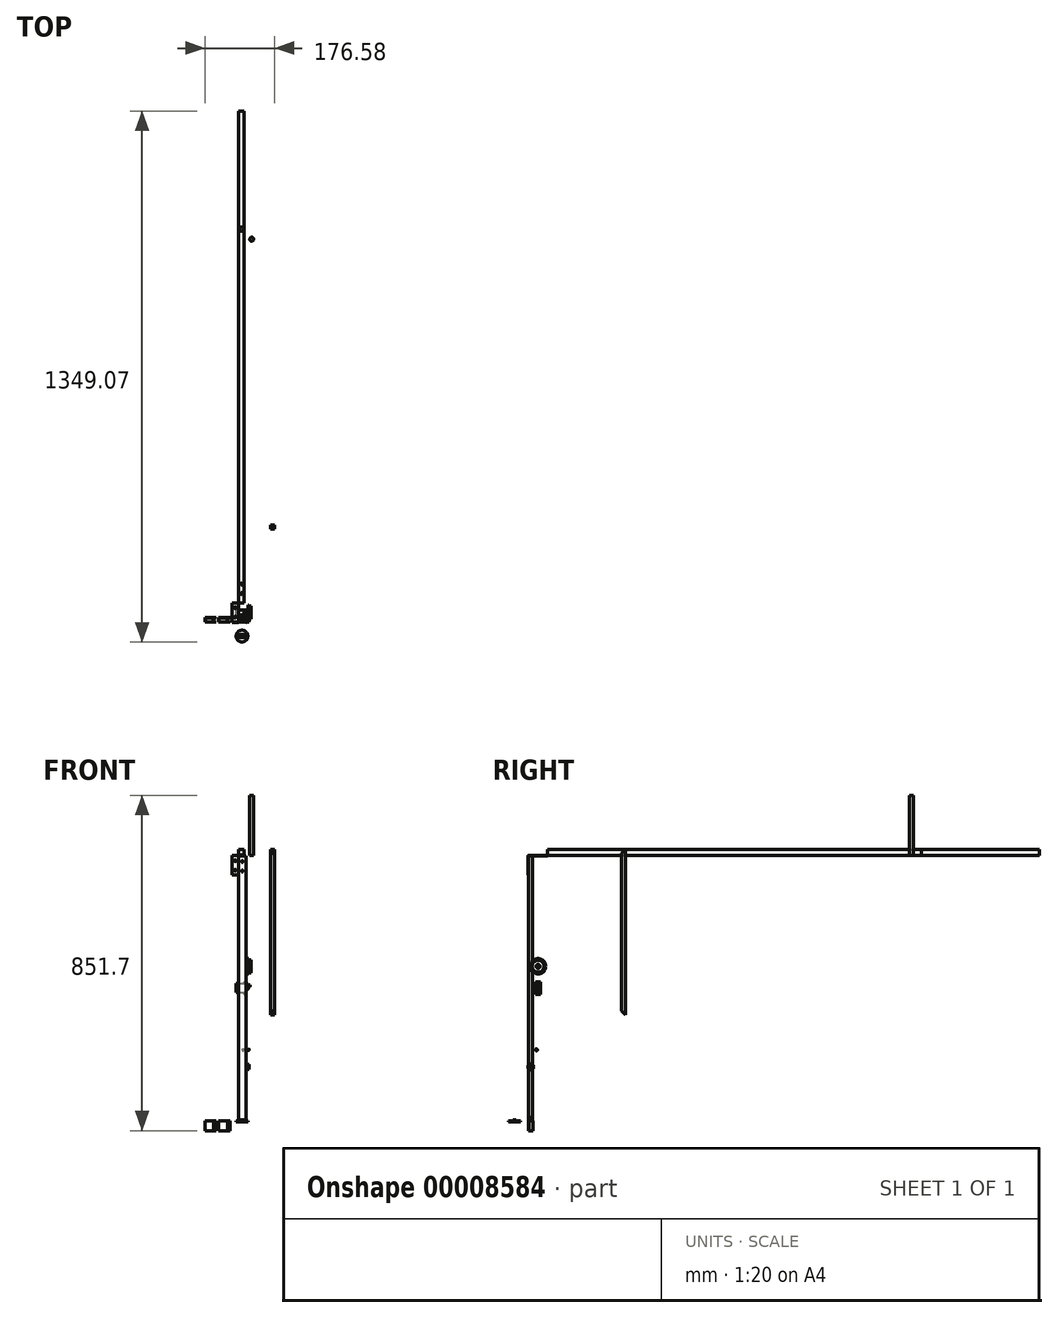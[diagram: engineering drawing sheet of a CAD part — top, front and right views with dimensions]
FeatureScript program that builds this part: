
annotation { "Feature Type Name" : "Feature", "Feature Type Description" : "" }
export const myFeature = defineFeature(function(context is Context, id is Id, definition is map)
    precondition{}
    {
        {
            var Q0;
            Q0=qCreatedBy(makeId("Front.planeOp"),FACE);
            var sketch = newSketch(context, id + "F0", { "sketchPlane" : qUnion([Q0])});
            skLineSegment(sketch, "E0.rect.bottom", {"start": v(-7.5, 7.5) * mm, "end": v(7.5, 7.5) * mm});
            skLineSegment(sketch, "E0.rect.top", {"start": v(-7.5, -7.5) * mm, "end": v(7.5, -7.5) * mm});
            skLineSegment(sketch, "E0.rect.left", {"start": v(-7.5, 7.5) * mm, "end": v(-7.5, -7.5) * mm});
            skLineSegment(sketch, "E0.rect.right", {"start": v(7.5, 7.5) * mm, "end": v(7.5, -7.5) * mm});
            skPoint(sketch, "E0.rect.middle", {"position": v(0, 0) * mm});
            skLineSegment(sketch, "E1.rect.bottom", {"start": v(-7, 7) * mm, "end": v(7, 7) * mm});
            skLineSegment(sketch, "E1.rect.top", {"start": v(-7, -7) * mm, "end": v(7, -7) * mm});
            skLineSegment(sketch, "E1.rect.left", {"start": v(-7, 7) * mm, "end": v(-7, -7) * mm});
            skLineSegment(sketch, "E1.rect.right", {"start": v(7, 7) * mm, "end": v(7, -7) * mm});
            skSolve(sketch);
        }
        {
            var Q0;
            Q0 = qSketchRegion(id + "F0", true);
            extrude(context, id + "F1", {"entities" : qUnion([Q0]), "depth" : 950 * mm});
        }
        {
            var Q0;
            Q0=makeQuery(id+"F1.opExtrude","SWEPT_FACE",FACE,{"disambiguationData":[OSD([sQuery(id+"F0.wireOp",EDGE,"E0.rect.left")])]});
            var sketch = newSketch(context, id + "F2", { "sketchPlane" : qUnion([Q0])});
            skLineSegment(sketch, "E2.bottom", {"start": v(998.04, -7.5) * mm, "end": v(950, -7.5) * mm});
            skLineSegment(sketch, "E2.top", {"start": v(998, -9.5) * mm, "end": v(950, -9.5) * mm});
            skLineSegment(sketch, "E2.right", {"start": v(950, -7.5) * mm, "end": v(950, -9.5) * mm});
            skLineSegment(sketch, "E3.top", {"start": v(1000, -57.5) * mm, "end": v(998, -57.5) * mm});
            skLineSegment(sketch, "E3.left", {"start": v(1000, -9.5) * mm, "end": v(1000, -57.5) * mm});
            skLineSegment(sketch, "E3.right", {"start": v(998, -9.5) * mm, "end": v(998, -57.5) * mm});
            skArc(sketch, "E4", {"start": v(1000, -9.5) * mm, "mid": v(999.4, -8.07) * mm, "end": v(997.96, -7.5) * mm});
            skSolve(sketch);
        }
        {
            var Q0;
            Q0 = qSketchRegion(id + "F2", true);
            extrude(context, id + "F3", {"entities" : qUnion([Q0]), "depth" : 16.4 * mm});
        }
        {
            var Q0;
            Q0=makeQuery(id+"F3.opExtrude","SWEPT_FACE",FACE,{"disambiguationData":[OSD([sQuery(id+"F2.wireOp",EDGE,"E3.left")])]});
            var sketch = newSketch(context, id + "F4", { "sketchPlane" : qUnion([Q0])});
            skCircle(sketch, "E5", {"center": v(-15.7, -21.5) * mm, "radius": 2.3 * mm});
            skCircle(sketch, "E6", {"center": v(-15.7, -45.5) * mm, "radius": 2.3 * mm});
            skSolve(sketch);
        }
        {
            var Q0;
            Q0 = qSketchRegion(id + "F4", true);
            extrude(context, id + "F5", {"entities" : qUnion([Q0]), "operationType" : NewBodyOperationType.REMOVE, "oppositeDirection" : true, "depth" : 25 * mm});
        }
        {
            var Q0;
            Q0=makeQuery(id+"F3.opExtrude","SWEPT_FACE",FACE,{"disambiguationData":[OSD([sQuery(id+"F2.wireOp",EDGE,"E2.bottom")])]});
            var sketch = newSketch(context, id + "F6", { "sketchPlane" : qUnion([Q0])});
            skCircle(sketch, "E7", {"center": v(0, 12) * mm, "radius": 2.3 * mm});
            skCircle(sketch, "E8", {"center": v(0, -12) * mm, "radius": 2.3 * mm});
            skCircle(sketch, "E9", {"center": v(-15.7, -985.97) * mm, "radius": 2.3 * mm});
            skCircle(sketch, "E10", {"center": v(-15.7, -961.99) * mm, "radius": 2.3 * mm});
            skSolve(sketch);
        }
        {
            var Q0;
            Q0=makeQuery(id+"F6.imprint","IMPRINT",FACE,{"disambiguationData":[TD([[makeQuery(id+"F6.imprint","IMPRINT",EDGE,{"derivedFrom":sQuery(id+"F6.wireOp",EDGE,"E9")}),1.0]])]});
            var Q1;
            Q1=makeQuery(id+"F6.imprint","IMPRINT",FACE,{"disambiguationData":[TD([[makeQuery(id+"F6.imprint","IMPRINT",EDGE,{"derivedFrom":sQuery(id+"F6.wireOp",EDGE,"E10")}),1.0]])]});
            extrude(context, id + "F7", {"entities" : qUnion([Q0, Q1]), "operationType" : NewBodyOperationType.REMOVE, "oppositeDirection" : true, "depth" : 3 * mm});
        }
        {
            var Q0;
            Q0=makeQuery(id+"F3.opExtrude","SWEPT_FACE",FACE,{"disambiguationData":[OSD([sQuery(id+"F2.wireOp",EDGE,"E2.top")])]});
            var sketch = newSketch(context, id + "F8", { "sketchPlane" : qUnion([Q0])});
            skLineSegment(sketch, "E11.bottom", {"start": v(-7.5, 998) * mm, "end": v(12.5, 998) * mm});
            skLineSegment(sketch, "E11.top", {"start": v(-7.5, 988) * mm, "end": v(12.5, 988) * mm});
            skLineSegment(sketch, "E11.left", {"start": v(-7.5, 998) * mm, "end": v(-7.5, 988) * mm});
            skLineSegment(sketch, "E11.right", {"start": v(12.5, 998) * mm, "end": v(12.5, 988) * mm});
            skLineSegment(sketch, "E12.rect.bottom", {"start": v(-6.75, 988.75) * mm, "end": v(11.75, 988.75) * mm});
            skLineSegment(sketch, "E12.rect.top", {"start": v(-6.75, 997.25) * mm, "end": v(11.75, 997.25) * mm});
            skLineSegment(sketch, "E12.rect.left", {"start": v(-6.75, 988.75) * mm, "end": v(-6.75, 997.25) * mm});
            skLineSegment(sketch, "E12.rect.right", {"start": v(11.75, 988.75) * mm, "end": v(11.75, 997.25) * mm});
            skPoint(sketch, "E12.rect.middle", {"position": v(2.5, 993) * mm});
            skSolve(sketch);
        }
        {
            var Q0;
            Q0=makeQuery(id+"F8.imprint","IMPRINT",FACE,{"disambiguationData":[TD([[makeQuery(id+"F8.imprint","IMPRINT",EDGE,{"derivedFrom":sQuery(id+"F8.wireOp",EDGE,"E11.bottom")}),-1.0]])]});
            extrude(context, id + "F9", {"entities" : qUnion([Q0]), "depth" : 673 * mm});
        }
        {
            var Q0;
            Q0=makeQuery(id+"F9.opExtrude","SWEPT_FACE",FACE,{"disambiguationData":[OSD([sQuery(id+"F8.wireOp",EDGE,"E11.bottom")])]});
            var sketch = newSketch(context, id + "F10", { "sketchPlane" : qUnion([Q0])});
            skCircle(sketch, "E13", {"center": v(2.5, -23.5) * mm, "radius": 2.3 * mm});
            skCircle(sketch, "E14", {"center": v(2.5, -47.5) * mm, "radius": 2.3 * mm});
            skSolve(sketch);
        }
        {
            var Q0;
            Q0 = qSketchRegion(id + "F10", true);
            extrude(context, id + "F11", {"entities" : qUnion([Q0]), "operationType" : NewBodyOperationType.REMOVE, "oppositeDirection" : true, "depth" : 11 * mm});
        }
        {
            var Q0;
            Q0=makeQuery(id+"F1.opExtrude","SWEPT_FACE",FACE,{"disambiguationData":[OSD([sQuery(id+"F0.wireOp",EDGE,"E0.rect.top")])]});
            var sketch = newSketch(context, id + "F12", { "sketchPlane" : qUnion([Q0])});
            skCircle(sketch, "E15", {"center": v(0, 901.99) * mm, "radius": 2.3 * mm});
            skCircle(sketch, "E16", {"center": v(0, 925.97) * mm, "radius": 2.3 * mm});
            skLineSegment(sketch, "E17", {"start": v(0, 950) * mm, "end": v(0, 925.97) * mm});
            skLineSegment(sketch, "E18", {"start": v(0, 925.97) * mm, "end": v(0, 901.99) * mm});
            skSolve(sketch);
        }
        {
            var Q0;
            Q0=makeQuery(id+"F12.imprint","IMPRINT",FACE,{"disambiguationData":[TD([[makeQuery(id+"F12.imprint","IMPRINT",EDGE,{"derivedFrom":sQuery(id+"F12.wireOp",EDGE,"E15")}),1.0]])]});
            var Q1;
            Q1=makeQuery(id+"F12.imprint","IMPRINT",FACE,{"disambiguationData":[TD([[makeQuery(id+"F12.imprint","IMPRINT",EDGE,{"derivedFrom":sQuery(id+"F12.wireOp",EDGE,"E16")}),1.0]])]});
            extrude(context, id + "F13", {"entities" : qUnion([Q0, Q1]), "operationType" : NewBodyOperationType.REMOVE, "oppositeDirection" : true, "depth" : 25 * mm});
        }
        {
            var Q0;
            Q0=makeQuery(id+"F9.opExtrude","CAP_FACE",FACE,{"disambiguationData":[OSD([sQuery(id+"F8.wireOp",EDGE,"E11.bottom"),sQuery(id+"F8.wireOp",EDGE,"E11.top"),sQuery(id+"F8.wireOp",EDGE,"E11.left"),sQuery(id+"F8.wireOp",EDGE,"E11.right"),sQuery(id+"F8.wireOp",EDGE,"E12.rect.bottom"),sQuery(id+"F8.wireOp",EDGE,"E12.rect.top"),sQuery(id+"F8.wireOp",EDGE,"E12.rect.left"),sQuery(id+"F8.wireOp",EDGE,"E12.rect.right")])],"isStart":false});
            var sketch = newSketch(context, id + "F14", { "sketchPlane" : qUnion([Q0])});
            skCircle(sketch, "E19", {"center": v(1.66, 1034.07) * mm, "radius": 15 * mm});
            skSolve(sketch);
        }
        {
            var Q0;
            Q0 = qSketchRegion(id + "F14", true);
            extrude(context, id + "F15", {"entities" : qUnion([Q0]), "depth" : 2 * mm});
        }
        {
            var Q0;
            Q0=makeQuery(id+"F15.opExtrude","CAP_FACE",FACE,{"disambiguationData":[OSD([sQuery(id+"F14.wireOp",EDGE,"E19")])],"isStart":true});
            var sketch = newSketch(context, id + "F16", { "sketchPlane" : qUnion([Q0])});
            skLineSegment(sketch, "E20.rect.bottom", {"start": v(-7.59, -1038.32) * mm, "end": v(10.91, -1038.32) * mm});
            skLineSegment(sketch, "E20.rect.top", {"start": v(-7.59, -1029.82) * mm, "end": v(10.91, -1029.82) * mm});
            skLineSegment(sketch, "E20.rect.left", {"start": v(-7.59, -1038.32) * mm, "end": v(-7.59, -1029.82) * mm});
            skLineSegment(sketch, "E20.rect.right", {"start": v(10.91, -1038.32) * mm, "end": v(10.91, -1029.82) * mm});
            skPoint(sketch, "E20.rect.middle", {"position": v(1.66, -1034.07) * mm});
            skSolve(sketch);
        }
        {
            var Q0;
            Q0 = qSketchRegion(id + "F16", true);
            extrude(context, id + "F17", {"entities" : qUnion([Q0]), "operationType" : NewBodyOperationType.ADD, "depth" : 3 * mm});
        }
        {
            var Q0;
            Q0=makeQuery(id+"F9.opExtrude","CAP_FACE",FACE,{"disambiguationData":[OSD([sQuery(id+"F8.wireOp",EDGE,"E11.bottom"),sQuery(id+"F8.wireOp",EDGE,"E11.top"),sQuery(id+"F8.wireOp",EDGE,"E11.left"),sQuery(id+"F8.wireOp",EDGE,"E11.right"),sQuery(id+"F8.wireOp",EDGE,"E12.rect.bottom"),sQuery(id+"F8.wireOp",EDGE,"E12.rect.top"),sQuery(id+"F8.wireOp",EDGE,"E12.rect.left"),sQuery(id+"F8.wireOp",EDGE,"E12.rect.right")])],"isStart":false});
            var sketch = newSketch(context, id + "F18", { "sketchPlane" : qUnion([Q0])});
            skLineSegment(sketch, "E21.rect.bottom", {"start": v(-56.56, 987.8) * mm, "end": v(-36.56, 987.8) * mm});
            skLineSegment(sketch, "E21.rect.top", {"start": v(-56.56, 997.8) * mm, "end": v(-36.56, 997.8) * mm});
            skLineSegment(sketch, "E21.rect.left", {"start": v(-56.56, 987.8) * mm, "end": v(-56.56, 997.8) * mm});
            skLineSegment(sketch, "E21.rect.right", {"start": v(-36.56, 987.8) * mm, "end": v(-36.56, 997.8) * mm});
            skPoint(sketch, "E21.rect.middle", {"position": v(-46.56, 992.8) * mm});
            skLineSegment(sketch, "E22.rect.bottom", {"start": v(-91.4, 987.8) * mm, "end": v(-71.4, 987.8) * mm});
            skLineSegment(sketch, "E22.rect.top", {"start": v(-91.4, 997.8) * mm, "end": v(-71.4, 997.8) * mm});
            skLineSegment(sketch, "E22.rect.left", {"start": v(-91.4, 987.8) * mm, "end": v(-91.4, 997.8) * mm});
            skLineSegment(sketch, "E22.rect.right", {"start": v(-71.4, 987.8) * mm, "end": v(-71.4, 997.8) * mm});
            skPoint(sketch, "E22.rect.middle", {"position": v(-81.4, 992.8) * mm});
            skLineSegment(sketch, "E23.rect.bottom", {"start": v(-92.4, 986.8) * mm, "end": v(-70.4, 986.8) * mm});
            skLineSegment(sketch, "E23.rect.top", {"start": v(-92.4, 998.8) * mm, "end": v(-70.4, 998.8) * mm});
            skLineSegment(sketch, "E23.rect.left", {"start": v(-92.4, 986.8) * mm, "end": v(-92.4, 998.8) * mm});
            skLineSegment(sketch, "E23.rect.right", {"start": v(-70.4, 986.8) * mm, "end": v(-70.4, 998.8) * mm});
            skLineSegment(sketch, "E24.rect.bottom", {"start": v(-57.56, 986.8) * mm, "end": v(-35.56, 986.8) * mm});
            skLineSegment(sketch, "E24.rect.top", {"start": v(-57.56, 998.8) * mm, "end": v(-35.56, 998.8) * mm});
            skLineSegment(sketch, "E24.rect.left", {"start": v(-57.56, 986.8) * mm, "end": v(-57.56, 998.8) * mm});
            skLineSegment(sketch, "E24.rect.right", {"start": v(-35.56, 986.8) * mm, "end": v(-35.56, 998.8) * mm});
            skSolve(sketch);
        }
        {
            var Q0;
            Q0 = qSketchRegion(id + "F18", true);
            extrude(context, id + "F19", {"entities" : qUnion([Q0]), "depth" : 24.7 * mm});
        }
        {
            var Q0;
            Q0=makeQuery(id+"F19.opExtrude","SWEPT_FACE",FACE,{"disambiguationData":[OSD([sQuery(id+"F18.wireOp",EDGE,"E23.rect.bottom")])]});
            var sketch = newSketch(context, id + "F20", { "sketchPlane" : qUnion([Q0])});
            skLineSegment(sketch, "E25", {"start": v(81.4, -528.03) * mm, "end": v(87.58, -521.85) * mm});
            skLineSegment(sketch, "E26", {"start": v(87.58, -521.85) * mm, "end": v(81.4, -515.68) * mm});
            skLineSegment(sketch, "E27", {"start": v(81.4, -515.68) * mm, "end": v(75.23, -521.85) * mm});
            skLineSegment(sketch, "E28", {"start": v(75.23, -521.85) * mm, "end": v(81.4, -528.03) * mm});
            skSolve(sketch);
        }
        {
            var Q0;
            Q0 = qSketchRegion(id + "F20", true);
            extrude(context, id + "F21", {"entities" : qUnion([Q0]), "operationType" : NewBodyOperationType.REMOVE, "oppositeDirection" : true, "depth" : 25 * mm});
        }
        {
            var Q0;
            Q0=makeQuery(id+"F19.opExtrude","CAP_FACE",FACE,{"disambiguationData":[OSD([sQuery(id+"F18.wireOp",EDGE,"E22.rect.bottom"),sQuery(id+"F18.wireOp",EDGE,"E22.rect.top"),sQuery(id+"F18.wireOp",EDGE,"E22.rect.left"),sQuery(id+"F18.wireOp",EDGE,"E22.rect.right"),sQuery(id+"F18.wireOp",EDGE,"E23.rect.bottom"),sQuery(id+"F18.wireOp",EDGE,"E23.rect.top"),sQuery(id+"F18.wireOp",EDGE,"E23.rect.left"),sQuery(id+"F18.wireOp",EDGE,"E23.rect.right")])],"isStart":false});
            var sketch = newSketch(context, id + "F22", { "sketchPlane" : qUnion([Q0])});
            skLineSegment(sketch, "E29", {"start": v(-70.4, 998.8) * mm, "end": v(-63.9, 998.8) * mm});
            skLineSegment(sketch, "E30", {"start": v(-63.9, 998.8) * mm, "end": v(-63.9, 997.8) * mm});
            skLineSegment(sketch, "E31", {"start": v(-63.9, 997.8) * mm, "end": v(-70.4, 997.8) * mm});
            skLineSegment(sketch, "E32", {"start": v(-70.4, 986.8) * mm, "end": v(-63.9, 986.8) * mm});
            skLineSegment(sketch, "E33", {"start": v(-63.9, 986.8) * mm, "end": v(-63.9, 987.8) * mm});
            skLineSegment(sketch, "E34", {"start": v(-63.9, 987.8) * mm, "end": v(-70.4, 987.8) * mm});
            skLineSegment(sketch, "E35", {"start": v(-35.56, 998.8) * mm, "end": v(-29.06, 998.8) * mm});
            skLineSegment(sketch, "E36", {"start": v(-29.06, 998.8) * mm, "end": v(-29.06, 997.8) * mm});
            skLineSegment(sketch, "E37", {"start": v(-29.06, 997.8) * mm, "end": v(-35.56, 997.8) * mm});
            skLineSegment(sketch, "E38", {"start": v(-35.56, 986.8) * mm, "end": v(-29.06, 986.8) * mm});
            skLineSegment(sketch, "E39", {"start": v(-29.06, 986.8) * mm, "end": v(-29.06, 987.8) * mm});
            skLineSegment(sketch, "E40", {"start": v(-29.06, 987.8) * mm, "end": v(-35.56, 987.8) * mm});
            skLineSegment(sketch, "E41", {"start": v(-70.4, 998.8) * mm, "end": v(-70.4, 997.8) * mm});
            skLineSegment(sketch, "E42", {"start": v(-70.4, 987.8) * mm, "end": v(-70.4, 986.8) * mm});
            skLineSegment(sketch, "E43", {"start": v(-35.56, 987.8) * mm, "end": v(-35.56, 986.8) * mm});
            skLineSegment(sketch, "E44", {"start": v(-35.56, 998.8) * mm, "end": v(-35.56, 997.8) * mm});
            skSolve(sketch);
        }
        {
            var Q0;
            Q0 = qSketchRegion(id + "F22", true);
            extrude(context, id + "F23", {"entities" : qUnion([Q0]), "oppositeDirection" : true, "depth" : 24.7 * mm});
        }
        {
            var Q0;
            Q0=makeQuery(id+"F9.opExtrude","SWEPT_FACE",FACE,{"disambiguationData":[OSD([sQuery(id+"F8.wireOp",EDGE,"E11.right")])]});
            var sketch = newSketch(context, id + "F24", { "sketchPlane" : qUnion([Q0])});
            skCircle(sketch, "E45", {"center": v(-992.74, -545.12) * mm, "radius": 7.5 * mm});
            skSolve(sketch);
        }
        {
            var Q0;
            Q0 = qSketchRegion(id + "F24", true);
            extrude(context, id + "F25", {"entities" : qUnion([Q0]), "depth" : 1.1 * mm});
        }
        {
            var Q0;
            Q0=makeQuery(id+"F25.opExtrude","CAP_FACE",FACE,{"disambiguationData":[OSD([sQuery(id+"F24.wireOp",EDGE,"E45")])],"isStart":false});
            var sketch = newSketch(context, id + "F26", { "sketchPlane" : qUnion([Q0])});
            skCircle(sketch, "E46", {"center": v(-992.74, -545.12) * mm, "radius": 5.25 * mm});
            skSolve(sketch);
        }
        {
            var Q0;
            Q0 = qSketchRegion(id + "F26", true);
            extrude(context, id + "F27", {"entities" : qUnion([Q0]), "operationType" : NewBodyOperationType.ADD, "depth" : 5.5 * mm});
        }
        {
            var Q0;
            Q0=makeQuery(id+"F27.opExtrude","CAP_FACE",FACE,{"disambiguationData":[OSD([sQuery(id+"F26.wireOp",EDGE,"E46")])],"isStart":false});
            var sketch = newSketch(context, id + "F28", { "sketchPlane" : qUnion([Q0])});
            skSolve(sketch);
        }
        {
            var Q0;
            Q0=makeQuery(id+"F28.imprint","IMPRINT",FACE,{"disambiguationData":[TD([[makeQuery(id+"F28.imprint","IMPRINT",EDGE,{"derivedFrom":makeQuery(id+"F27.opExtrude","CAP_EDGE",EDGE,{"disambiguationData":[OSD([sQuery(id+"F26.wireOp",EDGE,"E46")])],"isStart":false})}),1.0]])]});
            var sketch = newSketch(context, id + "F29", { "sketchPlane" : qUnion([Q0])});
            skCircle(sketch, "E47.0", {"center": v(-992.74, -545.12) * mm, "radius": 5.25 * mm});
            skLineSegment(sketch, "E48", {"start": v(-993.24, -539.89) * mm, "end": v(-992.32, -539.88) * mm});
            skLineSegment(sketch, "E49", {"start": v(-992.32, -539.88) * mm, "end": v(-992.53, -539.3) * mm});
            skLineSegment(sketch, "E50", {"start": v(-992.53, -539.3) * mm, "end": v(-993.01, -539.3) * mm});
            skLineSegment(sketch, "E51", {"start": v(-993.01, -539.3) * mm, "end": v(-993.24, -539.89) * mm});
            skSolve(sketch);
        }
        {
            var Q0;
            {var subQ1=sQuery(id+"F29.wireOp",EDGE,"E49");Q0=makeQuery(id+"F29.imprint","IMPRINT",FACE,{"disambiguationData":[TD([[makeQuery(id+"F29.imprint","IMPRINT",EDGE,{"derivedFrom":subQ1}),1.0]])]});}
            extrude(context, id + "F30", {"entities" : qUnion([Q0]), "oppositeDirection" : true, "depth" : 5.5 * mm});
        }
        {
            var Q0;
            Q0=makeQuery(id+"F30.opExtrude","SWEPT_BODY",BODY,{"disambiguationData":[OSD([sQuery(id+"F29.wireOp",EDGE,"E47.0"),sQuery(id+"F29.wireOp",EDGE,"E49"),sQuery(id+"F29.wireOp",EDGE,"E50"),sQuery(id+"F29.wireOp",EDGE,"E51")])]});
            var Q1;
            Q1=makeQuery(id+"F27.opExtrude","CAP_EDGE",EDGE,{"disambiguationData":[OSD([sQuery(id+"F26.wireOp",EDGE,"E46")])],"isStart":false});
            circularPattern(context, id + "F31", {"entities" : qUnion([Q0]), "axis" : qUnion([Q1]), "angle" : 10 * degree, "instanceCount" : 40, "computeTransformsWithoutBuiltin" : true});
        }
        {
            var Q0;
            Q0=makeQuery(id+"F25.opExtrude","CAP_FACE",FACE,{"disambiguationData":[OSD([sQuery(id+"F24.wireOp",EDGE,"E45")])],"isStart":true});
            var sketch = newSketch(context, id + "F32", { "sketchPlane" : qUnion([Q0])});
            skCircle(sketch, "E52", {"center": v(992.74, -545.12) * mm, "radius": 1.5 * mm});
            skSolve(sketch);
        }
        {
            var Q0;
            Q0 = qSketchRegion(id + "F32", true);
            extrude(context, id + "F33", {"entities" : qUnion([Q0]), "operationType" : NewBodyOperationType.REMOVE, "oppositeDirection" : true, "depth" : 25 * mm});
        }
        {
            var Q0;
            Q0=makeQuery(id+"F9.opExtrude","SWEPT_FACE",FACE,{"disambiguationData":[OSD([sQuery(id+"F8.wireOp",EDGE,"E11.right")])]});
            var sketch = newSketch(context, id + "F34", { "sketchPlane" : qUnion([Q0])});
            skLineSegment(sketch, "E53.bottom", {"start": v(-980.2, -333.62) * mm, "end": v(-968.2, -333.62) * mm});
            skLineSegment(sketch, "E53.top", {"start": v(-980.2, -356.12) * mm, "end": v(-968.2, -356.12) * mm});
            skLineSegment(sketch, "E53.left", {"start": v(-980.2, -333.62) * mm, "end": v(-980.2, -356.12) * mm});
            skLineSegment(sketch, "E53.right", {"start": v(-968.2, -333.62) * mm, "end": v(-968.2, -356.12) * mm});
            skSolve(sketch);
        }
        {
            var Q0;
            Q0 = qSketchRegion(id + "F34", true);
            extrude(context, id + "F35", {"entities" : qUnion([Q0]), "oppositeDirection" : true, "depth" : 26.5 * mm});
        }
        {
            var Q0;
            Q0=makeQuery(id+"F35.opExtrude","SWEPT_FACE",FACE,{"disambiguationData":[OSD([sQuery(id+"F34.wireOp",EDGE,"E53.right")])]});
            var sketch = newSketch(context, id + "F36", { "sketchPlane" : qUnion([Q0])});
            skLineSegment(sketch, "E54.bottom", {"start": v(-7, -356.12) * mm, "end": v(-8.5, -356.12) * mm});
            skLineSegment(sketch, "E54.top", {"start": v(-7, -361.12) * mm, "end": v(-8.5, -361.12) * mm});
            skLineSegment(sketch, "E54.left", {"start": v(-7, -356.12) * mm, "end": v(-7, -361.12) * mm});
            skLineSegment(sketch, "E54.right", {"start": v(-8.5, -356.12) * mm, "end": v(-8.5, -361.12) * mm});
            skLineSegment(sketch, "E55.bottom", {"start": v(-7, -333.62) * mm, "end": v(-8.5, -333.62) * mm});
            skLineSegment(sketch, "E55.top", {"start": v(-7, -328.62) * mm, "end": v(-8.5, -328.62) * mm});
            skLineSegment(sketch, "E55.left", {"start": v(-7, -333.62) * mm, "end": v(-7, -328.62) * mm});
            skLineSegment(sketch, "E55.right", {"start": v(-8.5, -333.62) * mm, "end": v(-8.5, -328.62) * mm});
            skSolve(sketch);
        }
        {
            var Q0;
            Q0 = qSketchRegion(id + "F36", true);
            extrude(context, id + "F37", {"entities" : qUnion([Q0]), "oppositeDirection" : true, "depth" : 12 * mm});
        }
        {
            var Q0;
            Q0=makeQuery(id+"F35.opExtrude","CAP_FACE",FACE,{"disambiguationData":[OSD([sQuery(id+"F34.wireOp",EDGE,"E53.bottom"),sQuery(id+"F34.wireOp",EDGE,"E53.top"),sQuery(id+"F34.wireOp",EDGE,"E53.left"),sQuery(id+"F34.wireOp",EDGE,"E53.right")])],"isStart":true});
            var sketch = newSketch(context, id + "F38", { "sketchPlane" : qUnion([Q0])});
            skLineSegment(sketch, "E56", {"start": v(-974.2, -333.62) * mm, "end": v(-974.2, -356.12) * mm});
            skCircle(sketch, "E57", {"center": v(-974.2, -339.6) * mm, "radius": 5.72 * mm});
            skSolve(sketch);
        }
        {
            var Q0;
            Q0 = qSketchRegion(id + "F38", true);
            extrude(context, id + "F39", {"entities" : qUnion([Q0]), "operationType" : NewBodyOperationType.ADD, "depth" : 4.5 * mm});
        }
        {
            var Q0;
            Q0=makeQuery(id+"F39.opExtrude","CAP_FACE",FACE,{"disambiguationData":[OSD([sQuery(id+"F38.wireOp",EDGE,"E57")])],"isStart":false});
            var sketch = newSketch(context, id + "F40", { "sketchPlane" : qUnion([Q0])});
            skCircle(sketch, "E58", {"center": v(-974.2, -339.6) * mm, "radius": 2 * mm});
            skSolve(sketch);
        }
        {
            var Q0;
            Q0 = qSketchRegion(id + "F40", true);
            extrude(context, id + "F41", {"entities" : qUnion([Q0]), "operationType" : NewBodyOperationType.ADD, "depth" : 4.5 * mm});
        }
        {
            var Q0;
            Q0=makeQuery(id+"F41.opExtrude","CAP_FACE",FACE,{"disambiguationData":[OSD([sQuery(id+"F40.wireOp",EDGE,"E58")])],"isStart":false});
            var sketch = newSketch(context, id + "F42", { "sketchPlane" : qUnion([Q0])});
            skLineSegment(sketch, "E59", {"start": v(-973.99, -341.58) * mm, "end": v(-974.14, -341.98) * mm});
            skLineSegment(sketch, "E60", {"start": v(-974.14, -341.98) * mm, "end": v(-974.35, -341.98) * mm});
            skLineSegment(sketch, "E61", {"start": v(-974.35, -341.98) * mm, "end": v(-974.5, -341.57) * mm});
            skLineSegment(sketch, "E62", {"start": v(-974.5, -341.57) * mm, "end": v(-973.99, -341.58) * mm});
            skSolve(sketch);
        }
        {
            var Q0;
            Q0 = qSketchRegion(id + "F42", true);
            extrude(context, id + "F43", {"entities" : qUnion([Q0]), "oppositeDirection" : true, "depth" : 4.5 * mm});
        }
        {
            var Q0;
            Q0=makeQuery(id+"F43.opExtrude","SWEPT_BODY",BODY,{"disambiguationData":[OSD([sQuery(id+"F42.wireOp",EDGE,"E59"),sQuery(id+"F42.wireOp",EDGE,"E60"),sQuery(id+"F42.wireOp",EDGE,"E61"),sQuery(id+"F42.wireOp",EDGE,"E62")])]});
            var Q1;
            Q1=makeQuery(id+"F41.opExtrude","CAP_EDGE",EDGE,{"disambiguationData":[OSD([sQuery(id+"F40.wireOp",EDGE,"E58")])],"isStart":false});
            circularPattern(context, id + "F44", {"entities" : qUnion([Q0]), "axis" : qUnion([Q1]), "angle" : 20 * degree, "instanceCount" : 30, "computeTransformsWithoutBuiltin" : true});
        }
        {
            var Q0;
            Q0=makeQuery(id+"F35.opExtrude","SWEPT_BODY",BODY,{"disambiguationData":[OSD([sQuery(id+"F34.wireOp",EDGE,"E53.bottom"),sQuery(id+"F34.wireOp",EDGE,"E53.top"),sQuery(id+"F34.wireOp",EDGE,"E53.left"),sQuery(id+"F34.wireOp",EDGE,"E53.right")])]});
            var Q1;
            Q1=makeQuery(id+"F37.opExtrude","SWEPT_BODY",BODY,{"disambiguationData":[OSD([sQuery(id+"F36.wireOp",EDGE,"E54.bottom"),sQuery(id+"F36.wireOp",EDGE,"E54.top"),sQuery(id+"F36.wireOp",EDGE,"E54.left"),sQuery(id+"F36.wireOp",EDGE,"E54.right")])]});
            var Q2;
            Q2=makeQuery(id+"F37.opExtrude","SWEPT_BODY",BODY,{"disambiguationData":[OSD([sQuery(id+"F36.wireOp",EDGE,"E55.bottom"),sQuery(id+"F36.wireOp",EDGE,"E55.top"),sQuery(id+"F36.wireOp",EDGE,"E55.left"),sQuery(id+"F36.wireOp",EDGE,"E55.right")])]});
            var Q3;
            Q3=makeQuery(id+"F44.opPattern","COPY",BODY,{"derivedFrom":makeQuery(id+"F43.opExtrude","SWEPT_BODY",BODY,{"disambiguationData":[OSD([sQuery(id+"F42.wireOp",EDGE,"E59"),sQuery(id+"F42.wireOp",EDGE,"E60"),sQuery(id+"F42.wireOp",EDGE,"E61"),sQuery(id+"F42.wireOp",EDGE,"E62")])]}),"instanceName":"14"});
            var Q4;
            Q4=makeQuery(id+"F44.opPattern","COPY",BODY,{"derivedFrom":makeQuery(id+"F43.opExtrude","SWEPT_BODY",BODY,{"disambiguationData":[OSD([sQuery(id+"F42.wireOp",EDGE,"E59"),sQuery(id+"F42.wireOp",EDGE,"E60"),sQuery(id+"F42.wireOp",EDGE,"E61"),sQuery(id+"F42.wireOp",EDGE,"E62")])]}),"instanceName":"12"});
            var Q5;
            Q5=makeQuery(id+"F44.opPattern","COPY",BODY,{"derivedFrom":makeQuery(id+"F43.opExtrude","SWEPT_BODY",BODY,{"disambiguationData":[OSD([sQuery(id+"F42.wireOp",EDGE,"E59"),sQuery(id+"F42.wireOp",EDGE,"E60"),sQuery(id+"F42.wireOp",EDGE,"E61"),sQuery(id+"F42.wireOp",EDGE,"E62")])]}),"instanceName":"13"});
            var Q6;
            Q6=makeQuery(id+"F44.opPattern","COPY",BODY,{"derivedFrom":makeQuery(id+"F43.opExtrude","SWEPT_BODY",BODY,{"disambiguationData":[OSD([sQuery(id+"F42.wireOp",EDGE,"E59"),sQuery(id+"F42.wireOp",EDGE,"E60"),sQuery(id+"F42.wireOp",EDGE,"E61"),sQuery(id+"F42.wireOp",EDGE,"E62")])]}),"instanceName":"17"});
            var Q7;
            Q7=makeQuery(id+"F44.opPattern","COPY",BODY,{"derivedFrom":makeQuery(id+"F43.opExtrude","SWEPT_BODY",BODY,{"disambiguationData":[OSD([sQuery(id+"F42.wireOp",EDGE,"E59"),sQuery(id+"F42.wireOp",EDGE,"E60"),sQuery(id+"F42.wireOp",EDGE,"E61"),sQuery(id+"F42.wireOp",EDGE,"E62")])]}),"instanceName":"15"});
            var Q8;
            Q8=makeQuery(id+"F44.opPattern","COPY",BODY,{"derivedFrom":makeQuery(id+"F43.opExtrude","SWEPT_BODY",BODY,{"disambiguationData":[OSD([sQuery(id+"F42.wireOp",EDGE,"E59"),sQuery(id+"F42.wireOp",EDGE,"E60"),sQuery(id+"F42.wireOp",EDGE,"E61"),sQuery(id+"F42.wireOp",EDGE,"E62")])]}),"instanceName":"11"});
            var Q9;
            Q9=makeQuery(id+"F44.opPattern","COPY",BODY,{"derivedFrom":makeQuery(id+"F43.opExtrude","SWEPT_BODY",BODY,{"disambiguationData":[OSD([sQuery(id+"F42.wireOp",EDGE,"E59"),sQuery(id+"F42.wireOp",EDGE,"E60"),sQuery(id+"F42.wireOp",EDGE,"E61"),sQuery(id+"F42.wireOp",EDGE,"E62")])]}),"instanceName":"16"});
            var Q10;
            Q10=makeQuery(id+"F44.opPattern","COPY",BODY,{"derivedFrom":makeQuery(id+"F43.opExtrude","SWEPT_BODY",BODY,{"disambiguationData":[OSD([sQuery(id+"F42.wireOp",EDGE,"E59"),sQuery(id+"F42.wireOp",EDGE,"E60"),sQuery(id+"F42.wireOp",EDGE,"E61"),sQuery(id+"F42.wireOp",EDGE,"E62")])]}),"instanceName":"5"});
            var Q11;
            Q11=makeQuery(id+"F43.opExtrude","SWEPT_BODY",BODY,{"disambiguationData":[OSD([sQuery(id+"F42.wireOp",EDGE,"E59"),sQuery(id+"F42.wireOp",EDGE,"E60"),sQuery(id+"F42.wireOp",EDGE,"E61"),sQuery(id+"F42.wireOp",EDGE,"E62")])]});
            var Q12;
            Q12=makeQuery(id+"F44.opPattern","COPY",BODY,{"derivedFrom":makeQuery(id+"F43.opExtrude","SWEPT_BODY",BODY,{"disambiguationData":[OSD([sQuery(id+"F42.wireOp",EDGE,"E59"),sQuery(id+"F42.wireOp",EDGE,"E60"),sQuery(id+"F42.wireOp",EDGE,"E61"),sQuery(id+"F42.wireOp",EDGE,"E62")])]}),"instanceName":"23"});
            var Q13;
            Q13=makeQuery(id+"F44.opPattern","COPY",BODY,{"derivedFrom":makeQuery(id+"F43.opExtrude","SWEPT_BODY",BODY,{"disambiguationData":[OSD([sQuery(id+"F42.wireOp",EDGE,"E59"),sQuery(id+"F42.wireOp",EDGE,"E60"),sQuery(id+"F42.wireOp",EDGE,"E61"),sQuery(id+"F42.wireOp",EDGE,"E62")])]}),"instanceName":"29"});
            var Q14;
            Q14=makeQuery(id+"F44.opPattern","COPY",BODY,{"derivedFrom":makeQuery(id+"F43.opExtrude","SWEPT_BODY",BODY,{"disambiguationData":[OSD([sQuery(id+"F42.wireOp",EDGE,"E59"),sQuery(id+"F42.wireOp",EDGE,"E60"),sQuery(id+"F42.wireOp",EDGE,"E61"),sQuery(id+"F42.wireOp",EDGE,"E62")])]}),"instanceName":"7"});
            var Q15;
            Q15=makeQuery(id+"F44.opPattern","COPY",BODY,{"derivedFrom":makeQuery(id+"F43.opExtrude","SWEPT_BODY",BODY,{"disambiguationData":[OSD([sQuery(id+"F42.wireOp",EDGE,"E59"),sQuery(id+"F42.wireOp",EDGE,"E60"),sQuery(id+"F42.wireOp",EDGE,"E61"),sQuery(id+"F42.wireOp",EDGE,"E62")])]}),"instanceName":"4"});
            var Q16;
            Q16=makeQuery(id+"F44.opPattern","COPY",BODY,{"derivedFrom":makeQuery(id+"F43.opExtrude","SWEPT_BODY",BODY,{"disambiguationData":[OSD([sQuery(id+"F42.wireOp",EDGE,"E59"),sQuery(id+"F42.wireOp",EDGE,"E60"),sQuery(id+"F42.wireOp",EDGE,"E61"),sQuery(id+"F42.wireOp",EDGE,"E62")])]}),"instanceName":"28"});
            var Q17;
            Q17=makeQuery(id+"F44.opPattern","COPY",BODY,{"derivedFrom":makeQuery(id+"F43.opExtrude","SWEPT_BODY",BODY,{"disambiguationData":[OSD([sQuery(id+"F42.wireOp",EDGE,"E59"),sQuery(id+"F42.wireOp",EDGE,"E60"),sQuery(id+"F42.wireOp",EDGE,"E61"),sQuery(id+"F42.wireOp",EDGE,"E62")])]}),"instanceName":"2"});
            var Q18;
            Q18=makeQuery(id+"F44.opPattern","COPY",BODY,{"derivedFrom":makeQuery(id+"F43.opExtrude","SWEPT_BODY",BODY,{"disambiguationData":[OSD([sQuery(id+"F42.wireOp",EDGE,"E59"),sQuery(id+"F42.wireOp",EDGE,"E60"),sQuery(id+"F42.wireOp",EDGE,"E61"),sQuery(id+"F42.wireOp",EDGE,"E62")])]}),"instanceName":"1"});
            var Q19;
            Q19=makeQuery(id+"F44.opPattern","COPY",BODY,{"derivedFrom":makeQuery(id+"F43.opExtrude","SWEPT_BODY",BODY,{"disambiguationData":[OSD([sQuery(id+"F42.wireOp",EDGE,"E59"),sQuery(id+"F42.wireOp",EDGE,"E60"),sQuery(id+"F42.wireOp",EDGE,"E61"),sQuery(id+"F42.wireOp",EDGE,"E62")])]}),"instanceName":"10"});
            var Q20;
            Q20=makeQuery(id+"F44.opPattern","COPY",BODY,{"derivedFrom":makeQuery(id+"F43.opExtrude","SWEPT_BODY",BODY,{"disambiguationData":[OSD([sQuery(id+"F42.wireOp",EDGE,"E59"),sQuery(id+"F42.wireOp",EDGE,"E60"),sQuery(id+"F42.wireOp",EDGE,"E61"),sQuery(id+"F42.wireOp",EDGE,"E62")])]}),"instanceName":"20"});
            var Q21;
            Q21=makeQuery(id+"F44.opPattern","COPY",BODY,{"derivedFrom":makeQuery(id+"F43.opExtrude","SWEPT_BODY",BODY,{"disambiguationData":[OSD([sQuery(id+"F42.wireOp",EDGE,"E59"),sQuery(id+"F42.wireOp",EDGE,"E60"),sQuery(id+"F42.wireOp",EDGE,"E61"),sQuery(id+"F42.wireOp",EDGE,"E62")])]}),"instanceName":"3"});
            var Q22;
            Q22=makeQuery(id+"F44.opPattern","COPY",BODY,{"derivedFrom":makeQuery(id+"F43.opExtrude","SWEPT_BODY",BODY,{"disambiguationData":[OSD([sQuery(id+"F42.wireOp",EDGE,"E59"),sQuery(id+"F42.wireOp",EDGE,"E60"),sQuery(id+"F42.wireOp",EDGE,"E61"),sQuery(id+"F42.wireOp",EDGE,"E62")])]}),"instanceName":"27"});
            var Q23;
            Q23=makeQuery(id+"F44.opPattern","COPY",BODY,{"derivedFrom":makeQuery(id+"F43.opExtrude","SWEPT_BODY",BODY,{"disambiguationData":[OSD([sQuery(id+"F42.wireOp",EDGE,"E59"),sQuery(id+"F42.wireOp",EDGE,"E60"),sQuery(id+"F42.wireOp",EDGE,"E61"),sQuery(id+"F42.wireOp",EDGE,"E62")])]}),"instanceName":"6"});
            var Q24;
            Q24=makeQuery(id+"F44.opPattern","COPY",BODY,{"derivedFrom":makeQuery(id+"F43.opExtrude","SWEPT_BODY",BODY,{"disambiguationData":[OSD([sQuery(id+"F42.wireOp",EDGE,"E59"),sQuery(id+"F42.wireOp",EDGE,"E60"),sQuery(id+"F42.wireOp",EDGE,"E61"),sQuery(id+"F42.wireOp",EDGE,"E62")])]}),"instanceName":"8"});
            var Q25;
            Q25=makeQuery(id+"F44.opPattern","COPY",BODY,{"derivedFrom":makeQuery(id+"F43.opExtrude","SWEPT_BODY",BODY,{"disambiguationData":[OSD([sQuery(id+"F42.wireOp",EDGE,"E59"),sQuery(id+"F42.wireOp",EDGE,"E60"),sQuery(id+"F42.wireOp",EDGE,"E61"),sQuery(id+"F42.wireOp",EDGE,"E62")])]}),"instanceName":"18"});
            var Q26;
            Q26=makeQuery(id+"F44.opPattern","COPY",BODY,{"derivedFrom":makeQuery(id+"F43.opExtrude","SWEPT_BODY",BODY,{"disambiguationData":[OSD([sQuery(id+"F42.wireOp",EDGE,"E59"),sQuery(id+"F42.wireOp",EDGE,"E60"),sQuery(id+"F42.wireOp",EDGE,"E61"),sQuery(id+"F42.wireOp",EDGE,"E62")])]}),"instanceName":"25"});
            var Q27;
            Q27=makeQuery(id+"F44.opPattern","COPY",BODY,{"derivedFrom":makeQuery(id+"F43.opExtrude","SWEPT_BODY",BODY,{"disambiguationData":[OSD([sQuery(id+"F42.wireOp",EDGE,"E59"),sQuery(id+"F42.wireOp",EDGE,"E60"),sQuery(id+"F42.wireOp",EDGE,"E61"),sQuery(id+"F42.wireOp",EDGE,"E62")])]}),"instanceName":"19"});
            var Q28;
            Q28=makeQuery(id+"F44.opPattern","COPY",BODY,{"derivedFrom":makeQuery(id+"F43.opExtrude","SWEPT_BODY",BODY,{"disambiguationData":[OSD([sQuery(id+"F42.wireOp",EDGE,"E59"),sQuery(id+"F42.wireOp",EDGE,"E60"),sQuery(id+"F42.wireOp",EDGE,"E61"),sQuery(id+"F42.wireOp",EDGE,"E62")])]}),"instanceName":"22"});
            var Q29;
            Q29=makeQuery(id+"F44.opPattern","COPY",BODY,{"derivedFrom":makeQuery(id+"F43.opExtrude","SWEPT_BODY",BODY,{"disambiguationData":[OSD([sQuery(id+"F42.wireOp",EDGE,"E59"),sQuery(id+"F42.wireOp",EDGE,"E60"),sQuery(id+"F42.wireOp",EDGE,"E61"),sQuery(id+"F42.wireOp",EDGE,"E62")])]}),"instanceName":"21"});
            var Q30;
            Q30=makeQuery(id+"F44.opPattern","COPY",BODY,{"derivedFrom":makeQuery(id+"F43.opExtrude","SWEPT_BODY",BODY,{"disambiguationData":[OSD([sQuery(id+"F42.wireOp",EDGE,"E59"),sQuery(id+"F42.wireOp",EDGE,"E60"),sQuery(id+"F42.wireOp",EDGE,"E61"),sQuery(id+"F42.wireOp",EDGE,"E62")])]}),"instanceName":"9"});
            var Q31;
            Q31=makeQuery(id+"F44.opPattern","COPY",BODY,{"derivedFrom":makeQuery(id+"F43.opExtrude","SWEPT_BODY",BODY,{"disambiguationData":[OSD([sQuery(id+"F42.wireOp",EDGE,"E59"),sQuery(id+"F42.wireOp",EDGE,"E60"),sQuery(id+"F42.wireOp",EDGE,"E61"),sQuery(id+"F42.wireOp",EDGE,"E62")])]}),"instanceName":"24"});
            var Q32;
            Q32=makeQuery(id+"F44.opPattern","COPY",BODY,{"derivedFrom":makeQuery(id+"F43.opExtrude","SWEPT_BODY",BODY,{"disambiguationData":[OSD([sQuery(id+"F42.wireOp",EDGE,"E59"),sQuery(id+"F42.wireOp",EDGE,"E60"),sQuery(id+"F42.wireOp",EDGE,"E61"),sQuery(id+"F42.wireOp",EDGE,"E62")])]}),"instanceName":"26"});
            booleanBodies(context, id + "F45", {"operationType" : BooleanOperationType.UNION, "tools" : qUnion([Q0, Q1, Q2, Q3, Q4, Q5, Q6, Q7, Q8, Q9, Q10, Q11, Q12, Q13, Q14, Q15, Q16, Q17, Q18, Q19, Q20, Q21, Q22, Q23, Q24, Q25, Q26, Q27, Q28, Q29, Q30, Q31, Q32])});
        }
        {
            var Q0;
            Q0=makeQuery(id+"F37.opExtrude","SWEPT_FACE",FACE,{"disambiguationData":[OSD([sQuery(id+"F36.wireOp",EDGE,"E54.right")])]});
            var sketch = newSketch(context, id + "F46", { "sketchPlane" : qUnion([Q0])});
            skArc(sketch, "E63", {"start": v(-973.78, -360.4) * mm, "mid": v(-974.2, -358.7) * mm, "end": v(-974.63, -360.4) * mm});
            skLineSegment(sketch, "E64.rect.bottom", {"start": v(-974.63, -361.99) * mm, "end": v(-973.78, -361.99) * mm});
            skLineSegment(sketch, "E64.rect.left", {"start": v(-974.63, -361.99) * mm, "end": v(-974.63, -360.4) * mm});
            skLineSegment(sketch, "E64.rect.right", {"start": v(-973.78, -361.99) * mm, "end": v(-973.78, -360.4) * mm});
            skPoint(sketch, "E64.rect.middle", {"position": v(-974.2, -361.12) * mm});
            skPoint(sketch, "E65.trimOffspring.end.orphan", {"position": v(-974.2, -356.12) * mm});
            skSolve(sketch);
        }
        {
            var Q0;
            {var subQ5=sQuery(id+"F46.wireOp",EDGE,"E63");Q0=makeQuery(id+"F46.imprint","IMPRINT",FACE,{"disambiguationData":[TD([[makeQuery(id+"F46.imprint","IMPRINT",EDGE,{"derivedFrom":subQ5}),1.0]])]});}
            extrude(context, id + "F47", {"entities" : qUnion([Q0]), "operationType" : NewBodyOperationType.REMOVE, "oppositeDirection" : true, "depth" : 25 * mm});
        }
        {
            var Q0;
            Q0=makeQuery(id+"F37.opExtrude","SWEPT_FACE",FACE,{"disambiguationData":[OSD([sQuery(id+"F36.wireOp",EDGE,"E55.right")])]});
            var sketch = newSketch(context, id + "F48", { "sketchPlane" : qUnion([Q0])});
            skArc(sketch, "E66", {"start": v(0.42, -0.22) * mm, "mid": v(0, 1.48) * mm, "end": v(-0.42, -0.22) * mm});
            skLineSegment(sketch, "E67.rect.bottom", {"start": v(-0.42, -1.81) * mm, "end": v(0.42, -1.81) * mm});
            skLineSegment(sketch, "E67.rect.left", {"start": v(-0.42, -1.81) * mm, "end": v(-0.42, -0.22) * mm});
            skLineSegment(sketch, "E67.rect.right", {"start": v(0.42, -1.81) * mm, "end": v(0.42, -0.22) * mm});
            skPoint(sketch, "E67.rect.middle", {"position": v(0, -0.95) * mm});
            skPoint(sketch, "E68.trimOffspring.end.orphan", {"position": v(0, 4.05) * mm});
            skLineSegment(sketch, "E69.0.4", {"start": v(-980.2, -356.12) * mm, "end": v(-980.2, -361.12) * mm});
            skLineSegment(sketch, "E70.0.MirrorCS", {"start": v(-974.63, -328.62) * mm, "end": v(-974.63, -329.35) * mm});
            skLineSegment(sketch, "E71.0.MirrorCS", {"start": v(-973.78, -329.35) * mm, "end": v(-973.78, -328.62) * mm});
            skArc(sketch, "E72.0.MirrorCS", {"start": v(-974.63, -329.35) * mm, "mid": v(-974.2, -331.06) * mm, "end": v(-973.78, -329.35) * mm});
            skLineSegment(sketch, "E73", {"start": v(-973.78, -328.62) * mm, "end": v(-974.63, -328.62) * mm});
            skSolve(sketch);
        }
        {
            var Q0;
            Q0=makeQuery(id+"F48.imprint","IMPRINT",FACE,{"disambiguationData":[TD([[makeQuery(id+"F48.imprint","IMPRINT",EDGE,{"derivedFrom":sQuery(id+"F48.wireOp",EDGE,"E70.0.MirrorCS")}),1.0]])]});
            extrude(context, id + "F49", {"entities" : qUnion([Q0]), "operationType" : NewBodyOperationType.REMOVE, "oppositeDirection" : true, "depth" : 25 * mm});
        }
        {
            var Q0;
            Q0=makeQuery(id+"F35.opExtrude","CAP_FACE",FACE,{"disambiguationData":[OSD([sQuery(id+"F34.wireOp",EDGE,"E53.bottom"),sQuery(id+"F34.wireOp",EDGE,"E53.top"),sQuery(id+"F34.wireOp",EDGE,"E53.left"),sQuery(id+"F34.wireOp",EDGE,"E53.right")])],"isStart":true});
            var sketch = newSketch(context, id + "F50", { "sketchPlane" : qUnion([Q0])});
            skArc(sketch, "E74", {"start": v(-975.76, -345.1) * mm, "mid": v(-974.2, -348.9) * mm, "end": v(-972.65, -345.1) * mm});
            skArc(sketch, "E75.0", {"start": v(-975.76, -345.1) * mm, "mid": v(-974.2, -345.32) * mm, "end": v(-972.65, -345.1) * mm});
            skPoint(sketch, "E76.start.orphan", {"position": v(-974.2, -356.12) * mm});
            skSolve(sketch);
        }
        {
            var Q0;
            Q0=makeQuery(id+"F50.imprint","IMPRINT",FACE,{"disambiguationData":[TD([[makeQuery(id+"F50.imprint","IMPRINT",EDGE,{"derivedFrom":sQuery(id+"F50.wireOp",EDGE,"E74")}),1.0]])]});
            extrude(context, id + "F51", {"entities" : qUnion([Q0]), "operationType" : NewBodyOperationType.ADD, "depth" : 4 * mm});
        }
        {
            var Q0;
            {var subQ0=sQuery(id+"F34.wireOp",EDGE,"E53.bottom");var subQ1=sQuery(id+"F36.wireOp",EDGE,"E55.left");Q0=makeQuery(id+"F45.opBoolean","SPLIT",FACE,{"disambiguationData":[TD([makeQuery(id+"F37.opExtrude","SWEPT_FACE",FACE,{"disambiguationData":[OSD([subQ1])]})])],"derivedFrom":makeQuery(id+"F35.opExtrude","SWEPT_FACE",FACE,{"disambiguationData":[OSD([subQ0])]})});}
            var sketch = newSketch(context, id + "F52", { "sketchPlane" : qUnion([Q0])});
            skLineSegment(sketch, "E77.rect.bottom", {"start": v(-9.94, -972.45) * mm, "end": v(-11.26, -972.45) * mm});
            skLineSegment(sketch, "E77.rect.top", {"start": v(-9.94, -975.96) * mm, "end": v(-11.26, -975.96) * mm});
            skLineSegment(sketch, "E77.rect.left", {"start": v(-9.94, -972.45) * mm, "end": v(-9.94, -975.96) * mm});
            skLineSegment(sketch, "E77.rect.right", {"start": v(-11.26, -972.45) * mm, "end": v(-11.26, -975.96) * mm});
            skPoint(sketch, "E77.rect.middle", {"position": v(-10.6, -974.2) * mm});
            skSolve(sketch);
        }
        {
            var Q0;
            Q0 = qSketchRegion(id + "F52", true);
            extrude(context, id + "F53", {"entities" : qUnion([Q0]), "operationType" : NewBodyOperationType.REMOVE, "oppositeDirection" : true, "depth" : 5 * mm});
        }
        {
            var Q0;
            Q0=makeQuery(id+"F39.opExtrude","CAP_FACE",FACE,{"disambiguationData":[OSD([sQuery(id+"F38.wireOp",EDGE,"E57")])],"isStart":false});
            var sketch = newSketch(context, id + "F54", { "sketchPlane" : qUnion([Q0])});
            skCircle(sketch, "E78", {"center": v(-974.2, -289.6) * mm, "radius": 19.5 * mm});
            skSolve(sketch);
        }
        {
            var Q0;
            Q0 = qSketchRegion(id + "F54", true);
            extrude(context, id + "F55", {"entities" : qUnion([Q0]), "depth" : 1 * mm});
        }
        {
            var Q0;
            Q0=makeQuery(id+"F55.opExtrude","CAP_FACE",FACE,{"disambiguationData":[OSD([sQuery(id+"F54.wireOp",EDGE,"E78")])],"isStart":false});
            var sketch = newSketch(context, id + "F56", { "sketchPlane" : qUnion([Q0])});
            skCircle(sketch, "E79", {"center": v(-974.2, -289.6) * mm, "radius": 15 * mm});
            skCircle(sketch, "E80", {"center": v(-974.2, -289.6) * mm, "radius": 15.58 * mm});
            skSolve(sketch);
        }
        {
            var Q0;
            Q0 = qSketchRegion(id + "F56", true);
            extrude(context, id + "F57", {"entities" : qUnion([Q0]), "operationType" : NewBodyOperationType.ADD, "depth" : 6 * mm});
        }
        {
            var Q0;
            Q0=makeQuery(id+"F57.boolean.opBoolean","SPLIT",FACE,{"disambiguationData":[TD([makeQuery(id+"F57.opExtrude","SWEPT_FACE",FACE,{"disambiguationData":[OSD([sQuery(id+"F56.wireOp",EDGE,"E79")])]})])],"derivedFrom":makeQuery(id+"F55.opExtrude","CAP_FACE",FACE,{"disambiguationData":[OSD([sQuery(id+"F54.wireOp",EDGE,"E78")])],"isStart":false})});
            var sketch = newSketch(context, id + "F58", { "sketchPlane" : qUnion([Q0])});
            skCircle(sketch, "E81", {"center": v(-974.2, -289.6) * mm, "radius": 4.5 * mm});
            skSolve(sketch);
        }
        {
            var Q0;
            Q0 = qSketchRegion(id + "F58", true);
            extrude(context, id + "F59", {"entities" : qUnion([Q0]), "operationType" : NewBodyOperationType.REMOVE, "oppositeDirection" : true, "depth" : 2 * mm});
        }
        {
            var Q0;
            {var subQ0=sQuery(id+"F54.wireOp",EDGE,"E78");Q0=makeQuery(id+"F57.boolean.opBoolean","SPLIT",FACE,{"disambiguationData":[TD([makeQuery(id+"F55.opExtrude","SWEPT_FACE",FACE,{"disambiguationData":[OSD([subQ0])]})])],"derivedFrom":makeQuery(id+"F55.opExtrude","CAP_FACE",FACE,{"disambiguationData":[OSD([subQ0])],"isStart":false})});}
            var sketch = newSketch(context, id + "F60", { "sketchPlane" : qUnion([Q0])});
            skLineSegment(sketch, "E82", {"start": v(-958.66, -288.7) * mm, "end": v(-958.05, -288.98) * mm});
            skLineSegment(sketch, "E83", {"start": v(-958.05, -288.98) * mm, "end": v(-958.05, -289.58) * mm});
            skLineSegment(sketch, "E84", {"start": v(-958.05, -289.58) * mm, "end": v(-958.63, -289.87) * mm});
            skLineSegment(sketch, "E85", {"start": v(-958.63, -289.87) * mm, "end": v(-958.66, -288.7) * mm});
            skSolve(sketch);
        }
        {
            var Q0;
            Q0 = qSketchRegion(id + "F60", true);
            extrude(context, id + "F61", {"entities" : qUnion([Q0]), "depth" : 6 * mm});
        }
        {
            var Q0;
            Q0=makeQuery(id+"F61.opExtrude","SWEPT_BODY",BODY,{"disambiguationData":[OSD([sQuery(id+"F60.wireOp",EDGE,"E82"),sQuery(id+"F60.wireOp",EDGE,"E83"),sQuery(id+"F60.wireOp",EDGE,"E84"),sQuery(id+"F60.wireOp",EDGE,"E85")])]});
            var Q1;
            Q1=makeQuery(id+"F57.opExtrude","CAP_EDGE",EDGE,{"disambiguationData":[OSD([sQuery(id+"F56.wireOp",EDGE,"E80")])],"isStart":false});
            circularPattern(context, id + "F62", {"entities" : qUnion([Q0]), "axis" : qUnion([Q1]), "angle" : 5 * degree, "instanceCount" : 75, "computeTransformsWithoutBuiltin" : true});
        }
        {
            var Q0;
            Q0=makeQuery(id+"F57.boolean.opBoolean","SPLIT",FACE,{"disambiguationData":[TD([makeQuery(id+"F57.opExtrude","SWEPT_FACE",FACE,{"disambiguationData":[OSD([sQuery(id+"F56.wireOp",EDGE,"E79")])]})])],"derivedFrom":makeQuery(id+"F55.opExtrude","CAP_FACE",FACE,{"disambiguationData":[OSD([sQuery(id+"F54.wireOp",EDGE,"E78")])],"isStart":false})});
            var sketch = newSketch(context, id + "F63", { "sketchPlane" : qUnion([Q0])});
            skCircle(sketch, "E86", {"center": v(-974.2, -289.6) * mm, "radius": 5 * mm});
            skCircle(sketch, "E87", {"center": v(-974.2, -289.6) * mm, "radius": 4.5 * mm});
            skSolve(sketch);
        }
        {
            var Q0;
            Q0 = qSketchRegion(id + "F63", true);
            extrude(context, id + "F64", {"entities" : qUnion([Q0]), "operationType" : NewBodyOperationType.ADD, "depth" : 6 * mm});
        }
        {
            var Q0;
            Q0=makeQuery(id+"F9.opExtrude","SWEPT_FACE",FACE,{"disambiguationData":[OSD([sQuery(id+"F8.wireOp",EDGE,"E11.right")])]});
            var sketch = newSketch(context, id + "F65", { "sketchPlane" : qUnion([Q0])});
            skCircle(sketch, "E88", {"center": v(-993, -674.5) * mm, "radius": 1.5 * mm});
            skSolve(sketch);
        }
        {
            var Q0;
            Q0 = qSketchRegion(id + "F65", true);
            extrude(context, id + "F66", {"entities" : qUnion([Q0]), "operationType" : NewBodyOperationType.REMOVE, "oppositeDirection" : true, "depth" : 20 * mm});
        }
        {
            var Q0;
            Q0=makeQuery(id+"F9.opExtrude","SWEPT_FACE",FACE,{"disambiguationData":[OSD([sQuery(id+"F8.wireOp",EDGE,"E11.right")])]});
            var sketch = newSketch(context, id + "F67", { "sketchPlane" : qUnion([Q0])});
            skCircle(sketch, "E89", {"center": v(-978.43, -501.64) * mm, "radius": 1.5 * mm});
            skSolve(sketch);
        }
        {
            var Q0;
            Q0 = qSketchRegion(id + "F67", true);
            extrude(context, id + "F68", {"entities" : qUnion([Q0]), "depth" : 15 * mm, "symmetric" : true});
        }
        {
            var Q0;
            Q0=makeQuery(id+"F68.opExtrude","CAP_FACE",FACE,{"disambiguationData":[OSD([sQuery(id+"F67.wireOp",EDGE,"E89")])],"isStart":true});
            var sketch = newSketch(context, id + "F69", { "sketchPlane" : qUnion([Q0])});
            skCircle(sketch, "E90", {"center": v(978.43, -501.64) * mm, "radius": 2.5 * mm});
            skSolve(sketch);
        }
        {
            var Q0;
            Q0 = qSketchRegion(id + "F69", true);
            extrude(context, id + "F70", {"entities" : qUnion([Q0]), "operationType" : NewBodyOperationType.ADD, "depth" : 2 * mm});
        }
        {
            var Q0;
            Q0=makeQuery(id+"F70.opExtrude","CAP_FACE",FACE,{"disambiguationData":[OSD([sQuery(id+"F69.wireOp",EDGE,"E90")])],"isStart":false});
            var sketch = newSketch(context, id + "F71", { "sketchPlane" : qUnion([Q0])});
            skLineSegment(sketch, "E91.rect.bottom", {"start": v(980.93, -501.84) * mm, "end": v(978.63, -501.84) * mm});
            skLineSegment(sketch, "E91.rect.top", {"start": v(980.93, -501.44) * mm, "end": v(978.63, -501.44) * mm});
            skLineSegment(sketch, "E91.rect.left", {"start": v(980.93, -501.84) * mm, "end": v(980.93, -501.44) * mm});
            skLineSegment(sketch, "E91.rect.right", {"start": v(975.93, -501.84) * mm, "end": v(975.93, -501.44) * mm});
            skPoint(sketch, "E91.rect.middle", {"position": v(978.43, -501.64) * mm});
            skLineSegment(sketch, "E92.rect.bottom", {"start": v(978.63, -504.14) * mm, "end": v(978.23, -504.14) * mm});
            skLineSegment(sketch, "E92.rect.top", {"start": v(978.63, -499.14) * mm, "end": v(978.23, -499.14) * mm});
            skLineSegment(sketch, "E92.rect.left", {"start": v(978.63, -504.14) * mm, "end": v(978.63, -501.84) * mm});
            skLineSegment(sketch, "E92.rect.right", {"start": v(978.23, -504.14) * mm, "end": v(978.23, -501.84) * mm});
            skLineSegment(sketch, "E93.trimOffspring", {"start": v(978.63, -501.44) * mm, "end": v(978.63, -499.14) * mm});
            skLineSegment(sketch, "E94.trimOffspring", {"start": v(978.23, -501.84) * mm, "end": v(975.93, -501.84) * mm});
            skLineSegment(sketch, "E95.trimOffspring", {"start": v(978.23, -501.44) * mm, "end": v(975.93, -501.44) * mm});
            skLineSegment(sketch, "E96.trimOffspring", {"start": v(978.23, -501.44) * mm, "end": v(978.23, -499.14) * mm});
            skSolve(sketch);
        }
        {
            var Q0;
            Q0 = qSketchRegion(id + "F71", true);
            extrude(context, id + "F72", {"entities" : qUnion([Q0]), "operationType" : NewBodyOperationType.REMOVE, "oppositeDirection" : true, "depth" : 1 * mm});
        }
        {
            var Q0;
            {var subQ0=sQuery(id+"F69.wireOp",EDGE,"E90");Q0=makeQuery(id+"F72.boolean.opBoolean","SPLIT",EDGE,{"disambiguationData":[TD([makeQuery(id+"F72.opExtrude","SWEPT_FACE",FACE,{"disambiguationData":[OSD([sQuery(id+"F71.wireOp",EDGE,"E91.rect.top")])]})])],"derivedFrom":makeQuery(id+"F70.opExtrude","CAP_EDGE",EDGE,{"disambiguationData":[OSD([subQ0])],"isStart":false})});}
            var Q1;
            {var subQ0=sQuery(id+"F69.wireOp",EDGE,"E90");Q1=makeQuery(id+"F72.boolean.opBoolean","SPLIT",EDGE,{"disambiguationData":[TD([makeQuery(id+"F72.opExtrude","SWEPT_FACE",FACE,{"disambiguationData":[OSD([sQuery(id+"F71.wireOp",EDGE,"E95.trimOffspring")])]})])],"derivedFrom":makeQuery(id+"F70.opExtrude","CAP_EDGE",EDGE,{"disambiguationData":[OSD([subQ0])],"isStart":false})});}
            var Q2;
            {var subQ0=sQuery(id+"F69.wireOp",EDGE,"E90");Q2=makeQuery(id+"F72.boolean.opBoolean","SPLIT",EDGE,{"disambiguationData":[TD([makeQuery(id+"F72.opExtrude","SWEPT_FACE",FACE,{"disambiguationData":[OSD([sQuery(id+"F71.wireOp",EDGE,"E92.rect.right")])]})])],"derivedFrom":makeQuery(id+"F70.opExtrude","CAP_EDGE",EDGE,{"disambiguationData":[OSD([subQ0])],"isStart":false})});}
            var Q3;
            {var subQ0=sQuery(id+"F69.wireOp",EDGE,"E90");Q3=makeQuery(id+"F72.boolean.opBoolean","SPLIT",EDGE,{"disambiguationData":[TD([makeQuery(id+"F72.opExtrude","SWEPT_FACE",FACE,{"disambiguationData":[OSD([sQuery(id+"F71.wireOp",EDGE,"E91.rect.bottom")])]})])],"derivedFrom":makeQuery(id+"F70.opExtrude","CAP_EDGE",EDGE,{"disambiguationData":[OSD([subQ0])],"isStart":false})});}
            fillet(context, id + "F73", {"entities" : qUnion([Q0, Q1, Q2, Q3]), "radius" : 1 * mm, "tangentPropagation" : true, "allowEdgeOverflow" : false});
        }
        {
            var Q0;
            Q0=makeQuery(id+"F1.opExtrude","SWEPT_FACE",FACE,{"disambiguationData":[OSD([sQuery(id+"F0.wireOp",EDGE,"E0.rect.top")])]});
            var sketch = newSketch(context, id + "F74", { "sketchPlane" : qUnion([Q0])});
            skCircle(sketch, "E97", {"center": v(26.34, 25.9) * mm, "radius": 5 * mm});
            skSolve(sketch);
        }
        {
            var Q0;
            Q0 = qSketchRegion(id + "F74", true);
            extrude(context, id + "F75", {"entities" : qUnion([Q0]), "oppositeDirection" : true, "depth" : 152 * mm});
        }
        {
            var Q0;
            Q0 = qSketchRegion(id + "F0", true);
            extrude(context, id + "F76", {"entities" : qUnion([Q0]), "oppositeDirection" : true, "depth" : 300 * mm});
        }
        {
            var Q0;
            Q0=makeQuery(id+"F76.opExtrude","SWEPT_FACE",FACE,{"disambiguationData":[OSD([sQuery(id+"F0.wireOp",EDGE,"E0.rect.bottom")])]});
            var sketch = newSketch(context, id + "F77", { "sketchPlane" : qUnion([Q0])});
            skCircle(sketch, "E98", {"center": v(0, 0) * mm, "radius": 5 * mm});
            skSolve(sketch);
        }
        {
            var Q0;
            Q0 = qSketchRegion(id + "F77", true);
            extrude(context, id + "F78", {"entities" : qUnion([Q0]), "operationType" : NewBodyOperationType.REMOVE, "oppositeDirection" : true, "depth" : 25 * mm});
        }
        {
            var Q0;
            Q0=makeQuery(id+"F1.opExtrude","SWEPT_FACE",FACE,{"disambiguationData":[OSD([sQuery(id+"F0.wireOp",EDGE,"E0.rect.bottom")])]});
            var sketch = newSketch(context, id + "F79", { "sketchPlane" : qUnion([Q0])});
            skLineSegment(sketch, "E99.rect.bottom", {"start": v(74.17, -761.82) * mm, "end": v(84.17, -761.82) * mm});
            skLineSegment(sketch, "E99.rect.top", {"start": v(74.17, -751.82) * mm, "end": v(84.17, -751.82) * mm});
            skLineSegment(sketch, "E99.rect.left", {"start": v(74.17, -761.82) * mm, "end": v(74.17, -751.82) * mm});
            skLineSegment(sketch, "E99.rect.right", {"start": v(84.17, -761.82) * mm, "end": v(84.17, -751.82) * mm});
            skPoint(sketch, "E99.rect.middle", {"position": v(79.17, -756.82) * mm});
            skLineSegment(sketch, "E100.rect.bottom", {"start": v(74.67, -761.32) * mm, "end": v(83.67, -761.32) * mm});
            skLineSegment(sketch, "E100.rect.top", {"start": v(74.67, -752.32) * mm, "end": v(83.67, -752.32) * mm});
            skLineSegment(sketch, "E100.rect.left", {"start": v(74.67, -761.32) * mm, "end": v(74.67, -752.32) * mm});
            skLineSegment(sketch, "E100.rect.right", {"start": v(83.67, -761.32) * mm, "end": v(83.67, -752.32) * mm});
            skSolve(sketch);
        }
        {
            var Q0;
            Q0 = qSketchRegion(id + "F79", true);
            extrude(context, id + "F80", {"entities" : qUnion([Q0]), "oppositeDirection" : true, "depth" : 420 * mm});
        }
        {
            var Q0;
            Q0=makeQuery(id+"F80.opExtrude","SWEPT_FACE",FACE,{"disambiguationData":[OSD([sQuery(id+"F79.wireOp",EDGE,"E99.rect.right")])]});
            var sketch = newSketch(context, id + "F81", { "sketchPlane" : qUnion([Q0])});
            skLineSegment(sketch, "E101", {"start": v(-751.82, 7.5) * mm, "end": v(-761.82, -2.5) * mm});
            skLineSegment(sketch, "E102", {"start": v(-761.82, -2.5) * mm, "end": v(-761.82, 7.5) * mm});
            skLineSegment(sketch, "E103", {"start": v(-761.82, 7.5) * mm, "end": v(-751.82, 7.5) * mm});
            skSolve(sketch);
        }
        {
            var Q0;
            Q0 = qSketchRegion(id + "F81", true);
            extrude(context, id + "F82", {"entities" : qUnion([Q0]), "operationType" : NewBodyOperationType.REMOVE, "oppositeDirection" : true, "depth" : 10 * mm});
        }
        {
            var Q0;
            Q0=makeQuery(id+"F80.opExtrude","SWEPT_FACE",FACE,{"disambiguationData":[OSD([sQuery(id+"F79.wireOp",EDGE,"E99.rect.right")])]});
            var sketch = newSketch(context, id + "F83", { "sketchPlane" : qUnion([Q0])});
            skLineSegment(sketch, "E104", {"start": v(-751.82, -412.5) * mm, "end": v(-761.82, -402.5) * mm});
            skLineSegment(sketch, "E105", {"start": v(-761.82, -402.5) * mm, "end": v(-761.82, -412.5) * mm});
            skLineSegment(sketch, "E106", {"start": v(-761.82, -412.5) * mm, "end": v(-751.82, -412.5) * mm});
            skSolve(sketch);
        }
        {
            var Q0;
            Q0 = qSketchRegion(id + "F83", true);
            extrude(context, id + "F84", {"entities" : qUnion([Q0]), "operationType" : NewBodyOperationType.REMOVE, "oppositeDirection" : true, "depth" : 10 * mm});
        }
    });
